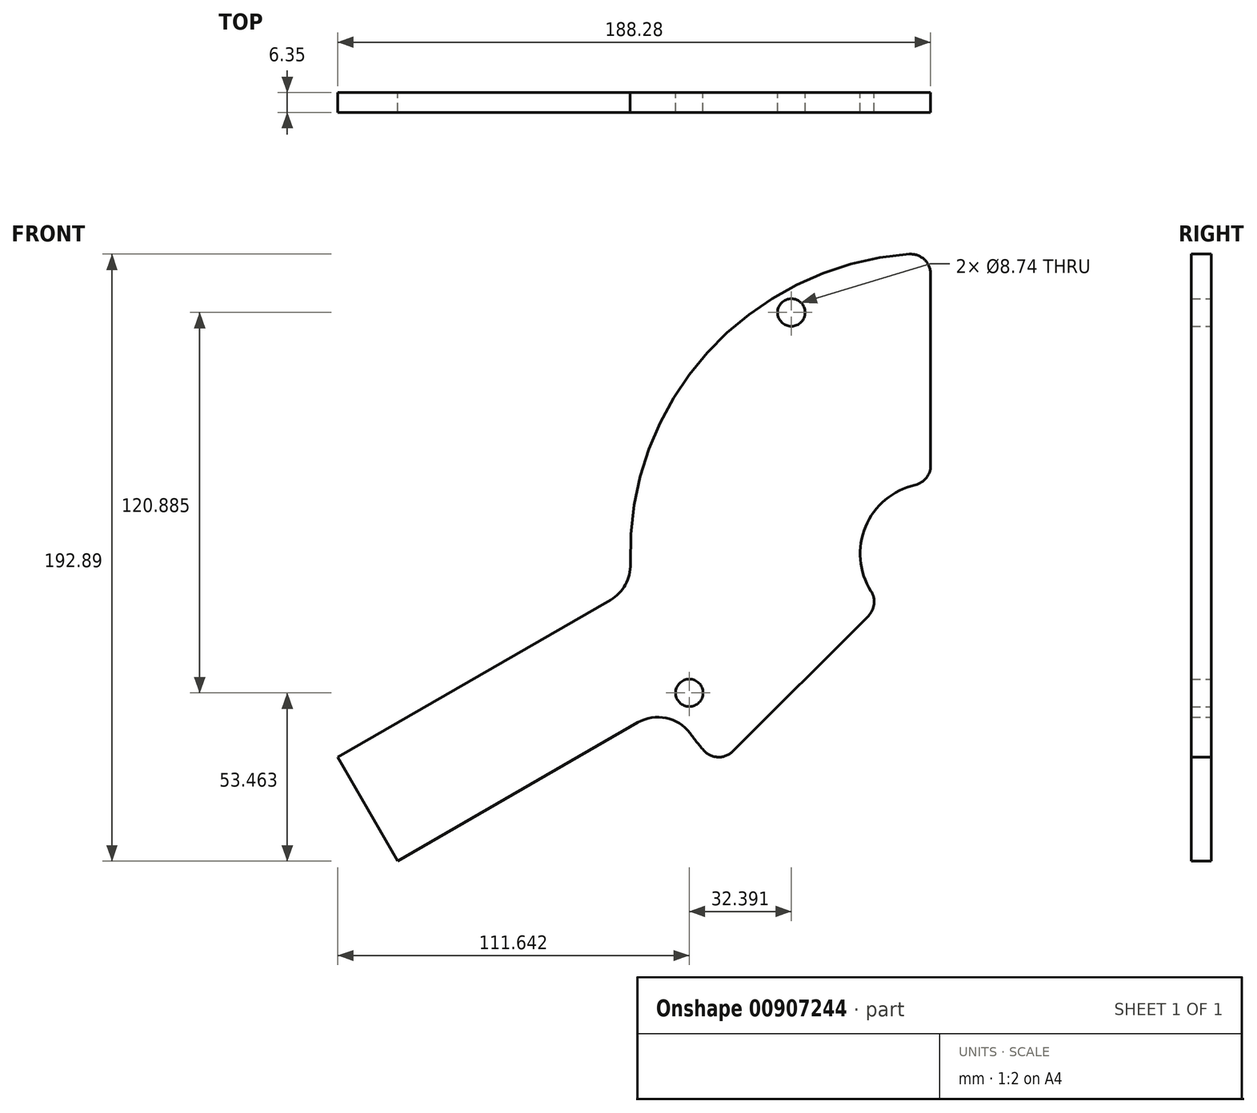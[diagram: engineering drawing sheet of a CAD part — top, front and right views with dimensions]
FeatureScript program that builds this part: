
annotation { "Feature Type Name" : "Feature", "Feature Type Description" : "" }
export const myFeature = defineFeature(function(context is Context, id is Id, definition is map)
    precondition{}
    {
        {
            var Q0;
            Q0=qCreatedBy(makeId("Front.planeOp"),FACE);
            var sketch = newSketch(context, id + "F0", { "sketchPlane" : qUnion([Q0])});
            skLineSegment(sketch, "E0", {"start": v(-82.62, -47.7) * mm, "end": v(-141.74, -81.83) * mm});
            skLineSegment(sketch, "E1", {"start": v(-141.74, -81.83) * mm, "end": v(-160.79, -48.84) * mm, "construction": true});
            skLineSegment(sketch, "E2", {"start": v(-160.79, -48.84) * mm, "end": v(-94.8, -10.74) * mm});
            skArc(sketch, "E3", {"start": v(0, 95.4) * mm, "mid": v(-71.15, 63.55) * mm, "end": v(-94.8, -10.74) * mm});
            skArc(sketch, "E4", {"start": v(0, 22.38) * mm, "mid": v(-20.67, 8.56) * mm, "end": v(-15.82, -15.82) * mm});
            skLineSegment(sketch, "E5", {"start": v(0, 0) * mm, "end": v(67.46, 67.46) * mm, "construction": true});
            skLineSegment(sketch, "E6", {"start": v(-15.82, -15.82) * mm, "end": v(-67.46, -67.46) * mm});
            skLineSegment(sketch, "E7", {"start": v(0, 0) * mm, "end": v(-82.62, -47.7) * mm, "construction": true});
            skArc(sketch, "E8.trimOffspring", {"start": v(-82.62, -47.7) * mm, "mid": v(-75.69, -58.08) * mm, "end": v(-67.46, -67.46) * mm});
            skLineSegment(sketch, "E9", {"start": v(0, 22.38) * mm, "end": v(0, 95.4) * mm});
            skLineSegment(sketch, "E10", {"start": v(-160.79, -48.84) * mm, "end": v(-188.28, -64.71) * mm});
            skLineSegment(sketch, "E11", {"start": v(-188.28, -64.71) * mm, "end": v(-169.23, -97.7) * mm});
            skLineSegment(sketch, "E12", {"start": v(-169.23, -97.7) * mm, "end": v(-141.74, -81.83) * mm});
            skSolve(sketch);
        }
        {
            var Q0;
            Q0=qSketchRegion(id+"F0",true);
            extrude(context, id + "F1", {"entities" : qUnion([Q0]), "depth" : 6.35 * mm, "offsetDistance" : 25.4 * mm});
        }
        {
            var Q0;
            Q0=makeQuery(id+"F1.opExtrude","CAP_FACE",FACE,{"disambiguationData":[OSD([sQuery(id+"F0.wireOp",EDGE,"E0"),sQuery(id+"F0.wireOp",EDGE,"E1"),sQuery(id+"F0.wireOp",EDGE,"E2"),sQuery(id+"F0.wireOp",EDGE,"E3"),sQuery(id+"F0.wireOp",EDGE,"E4"),sQuery(id+"F0.wireOp",EDGE,"E5"),sQuery(id+"F0.wireOp",EDGE,"E6"),sQuery(id+"F0.wireOp",EDGE,"E8.trimOffspring")])],"isStart":false});
            var sketch = newSketch(context, id + "F2", { "sketchPlane" : qUnion([Q0])});
            skLineSegment(sketch, "E13", {"start": v(0, 0) * mm, "end": v(82.62, 47.7) * mm, "construction": true});
            skLineSegment(sketch, "E14", {"start": v(0, 0) * mm, "end": v(-47.7, 82.62) * mm, "construction": true});
            skLineSegment(sketch, "E15", {"start": v(0, 0) * mm, "end": v(47.7, -82.62) * mm, "construction": true});
            skLineSegment(sketch, "E16", {"start": v(0, 0) * mm, "end": v(-82.62, -47.7) * mm, "construction": true});
            skCircle(sketch, "E17", {"center": v(-44.25, 76.64) * mm, "radius": 5.8 * mm, "construction": true});
            skCircle(sketch, "E18", {"center": v(-76.64, -44.25) * mm, "radius": 5.8 * mm, "construction": true});
            skLineSegment(sketch, "E19", {"start": v(-44.28, 76.7) * mm, "end": v(-76.7, -44.28) * mm, "construction": true});
            skLineSegment(sketch, "E20", {"start": v(-76.7, -44.28) * mm, "end": v(44.28, -76.7) * mm, "construction": true});
            skLineSegment(sketch, "E21", {"start": v(44.28, -76.7) * mm, "end": v(76.7, 44.28) * mm, "construction": true});
            skLineSegment(sketch, "E22", {"start": v(76.7, 44.28) * mm, "end": v(-44.28, 76.7) * mm, "construction": true});
            skSolve(sketch);
        }
        {
            var Q0;
            Q0=sQuery(id+"F2.wireOp",VERTEX,"E17.center");
            var Q1;
            Q1=sQuery(id+"F2.wireOp",VERTEX,"E18.center");
            var Q2;
            Q2=makeQuery(id+"F1.opExtrude","SWEPT_BODY",BODY,{"disambiguationData":[OSD([sQuery(id+"F0.wireOp",EDGE,"E0"),sQuery(id+"F0.wireOp",EDGE,"E1"),sQuery(id+"F0.wireOp",EDGE,"E2"),sQuery(id+"F0.wireOp",EDGE,"E3"),sQuery(id+"F0.wireOp",EDGE,"E4"),sQuery(id+"F0.wireOp",EDGE,"E5"),sQuery(id+"F0.wireOp",EDGE,"E6"),sQuery(id+"F0.wireOp",EDGE,"E8.trimOffspring")])]});
            hole(context, id + "F3", {"style" : HoleStyle.SIMPLE, "endStyle" : HoleEndStyle.THROUGH, "standardTappedOrClearance" : lookupTablePath({ "fit" : "Normal (ASME)", "standard" : "ANSI", "size" : "5/16", "type" : "Clearance" }), "standardBlindInLast" : lookupTablePath({ "fit" : "Normal", "standard" : "ANSI", "engagement" : "75%", "pitch" : "18 tpi", "size" : "5/16", "type" : "Clearance & tapped" }), "holeDiameter" : 8.74 * mm, "majorDiameter" : 6.35 * mm, "isTappedThrough" : true, "tappedDepth" : 8.47 * mm, "tapClearance" : 3, "locations" : qUnion([Q0, Q1]), "scope" : qUnion([Q2]), "startStyle" : HoleStartStyle.SKETCH});
        }
        {
            var Q0;
            Q0=makeQuery(id+"F1.opExtrude","SWEPT_EDGE",EDGE,{"disambiguationData":[OSD([sQuery(id+"F0.wireOp",EDGE,"E0"),sQuery(id+"F0.wireOp",EDGE,"E8.trimOffspring")])]});
            var Q1;
            Q1=makeQuery(id+"F1.opExtrude","SWEPT_EDGE",EDGE,{"disambiguationData":[OSD([sQuery(id+"F0.wireOp",EDGE,"E2"),sQuery(id+"F0.wireOp",EDGE,"E3")])]});
            fillet(context, id + "F4", {"entities" : qUnion([Q0, Q1]), "radius" : 12.7 * mm, "tangentPropagation" : true, "allowEdgeOverflow" : false});
        }
        {
            var Q0;
            Q0=makeQuery(id+"F1.opExtrude","SWEPT_EDGE",EDGE,{"disambiguationData":[OSD([sQuery(id+"F0.wireOp",EDGE,"E6"),sQuery(id+"F0.wireOp",EDGE,"E8.trimOffspring")])]});
            var Q1;
            Q1=makeQuery(id+"F1.opExtrude","SWEPT_EDGE",EDGE,{"disambiguationData":[OSD([sQuery(id+"F0.wireOp",EDGE,"E4"),sQuery(id+"F0.wireOp",EDGE,"E6")])]});
            var Q2;
            Q2=makeQuery(id+"F1.opExtrude","SWEPT_EDGE",EDGE,{"disambiguationData":[OSD([sQuery(id+"F0.wireOp",EDGE,"E4"),sQuery(id+"F0.wireOp",EDGE,"E9")])]});
            var Q3;
            Q3=makeQuery(id+"F1.opExtrude","SWEPT_EDGE",EDGE,{"disambiguationData":[OSD([sQuery(id+"F0.wireOp",EDGE,"E3"),sQuery(id+"F0.wireOp",EDGE,"E9")])]});
            fillet(context, id + "F5", {"entities" : qUnion([Q0, Q1, Q2, Q3]), "radius" : 6.35 * mm, "tangentPropagation" : true, "allowEdgeOverflow" : false});
        }
    });
